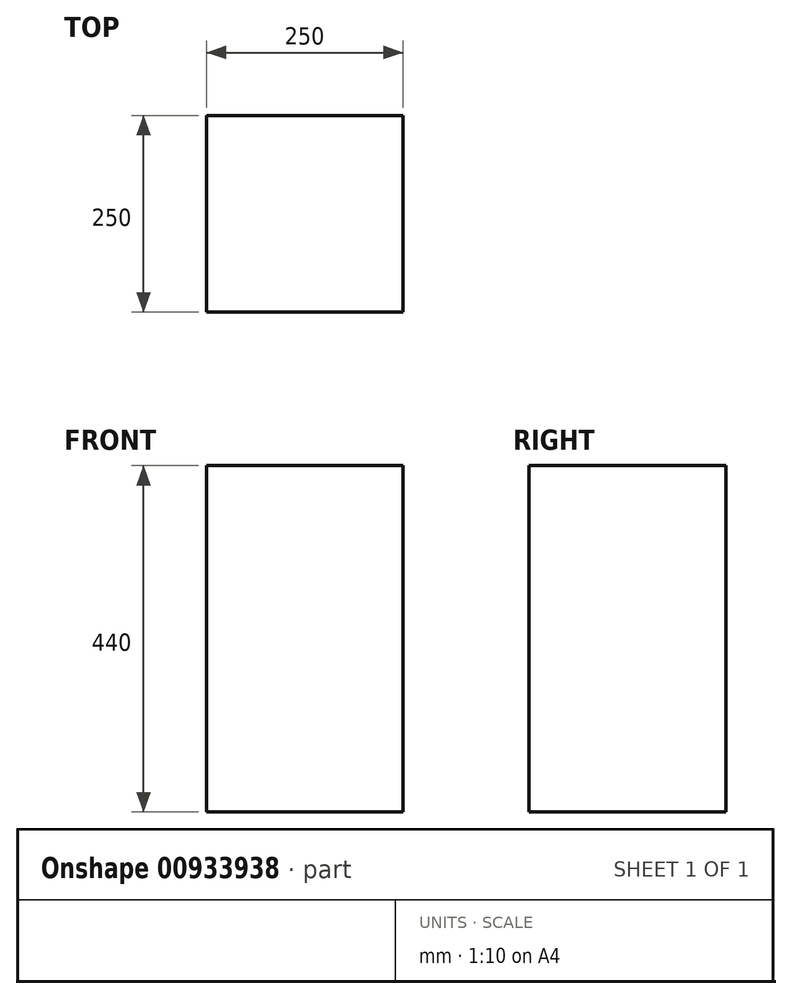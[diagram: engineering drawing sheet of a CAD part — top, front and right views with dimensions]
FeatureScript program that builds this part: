
annotation { "Feature Type Name" : "Feature", "Feature Type Description" : "" }
export const myFeature = defineFeature(function(context is Context, id is Id, definition is map)
    precondition{}
    {
        {
            var Q0;
            Q0=qCreatedBy(makeId("Front.planeOp"),FACE);
            var sketch = newSketch(context, id + "F0", { "sketchPlane" : qUnion([Q0])});
            skLineSegment(sketch, "E0", {"start": v(0, 0) * mm, "end": v(0, 220) * mm, "construction": true});
            skLineSegment(sketch, "E1", {"start": v(0, 0) * mm, "end": v(0, -220) * mm, "construction": true});
            skLineSegment(sketch, "E2", {"start": v(0, -220) * mm, "end": v(-125, -220) * mm, "construction": true});
            skLineSegment(sketch, "E3", {"start": v(-125, -220) * mm, "end": v(-125, 220) * mm, "construction": true});
            skLineSegment(sketch, "E4", {"start": v(-125, 220) * mm, "end": v(125, 220) * mm, "construction": true});
            skLineSegment(sketch, "E5", {"start": v(125, 220) * mm, "end": v(125, -220) * mm, "construction": true});
            skLineSegment(sketch, "E6", {"start": v(125, -220) * mm, "end": v(0, -220) * mm, "construction": true});
            skLineSegment(sketch, "E7.bottom", {"start": v(-125, 220) * mm, "end": v(125, 220) * mm});
            skLineSegment(sketch, "E7.top", {"start": v(-125, -220) * mm, "end": v(125, -220) * mm});
            skLineSegment(sketch, "E7.left", {"start": v(-125, 220) * mm, "end": v(-125, -220) * mm});
            skLineSegment(sketch, "E7.right", {"start": v(125, 220) * mm, "end": v(125, -220) * mm});
            skSolve(sketch);
        }
        {
            var Q0;
            Q0=makeQuery(id+"F0.imprint","IMPRINT",FACE,{"disambiguationData":[TD([[makeQuery(id+"F0.imprint","IMPRINT",EDGE,{"derivedFrom":sQuery(id+"F0.wireOp",EDGE,"E7.bottom")}),-1.0]])]});
            extrude(context, id + "F1", {"entities" : qUnion([Q0]), "depth" : 125 * mm, "offsetDistance" : 25 * mm, "hasSecondDirection" : true, "secondDirectionOppositeDirection" : true, "secondDirectionDepth" : 125 * mm});
        }
    });
